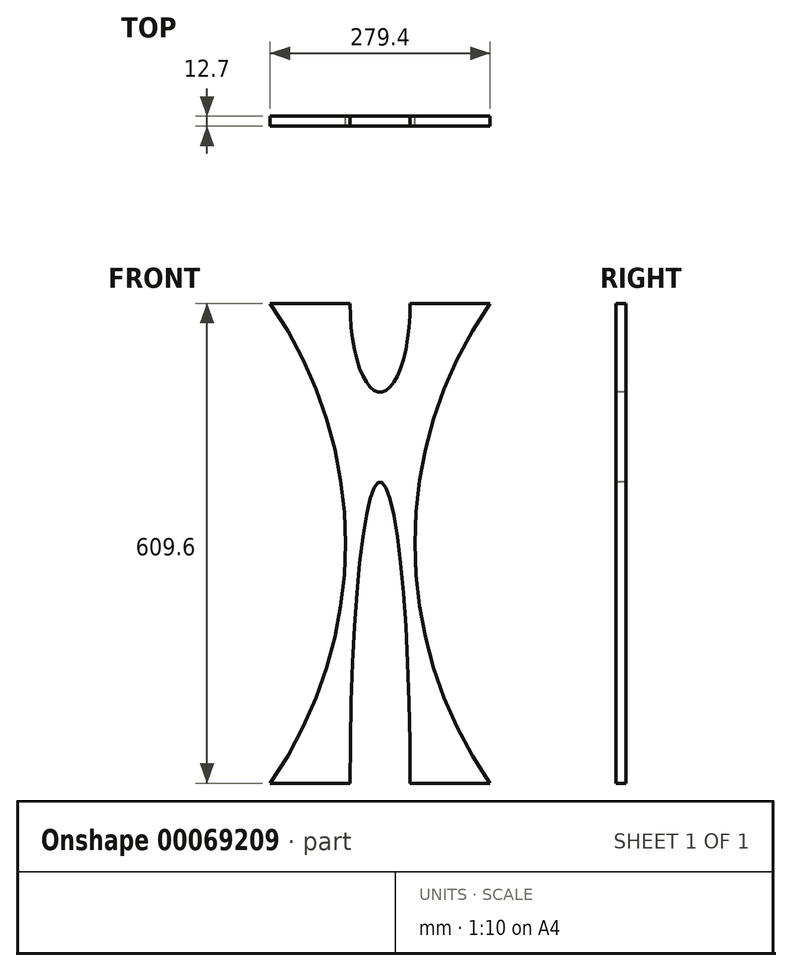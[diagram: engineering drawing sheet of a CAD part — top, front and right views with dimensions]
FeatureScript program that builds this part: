
annotation { "Feature Type Name" : "Feature", "Feature Type Description" : "" }
export const myFeature = defineFeature(function(context is Context, id is Id, definition is map)
    precondition{}
    {
        {
            var Q0;
            Q0=qCreatedBy(makeId("Front.planeOp"),FACE);
            var sketch = newSketch(context, id + "F0", { "sketchPlane" : qUnion([Q0])});
            skLineSegment(sketch, "E0", {"start": v(0, 0) * mm, "end": v(101.6, 0) * mm});
            skLineSegment(sketch, "E1", {"start": v(101.6, 609.6) * mm, "end": v(0, 609.6) * mm});
            skLineSegment(sketch, "E2", {"start": v(0, 0) * mm, "end": v(0, 704.65) * mm, "construction": true});
            skLineSegment(sketch, "E3", {"start": v(-38.1, 0) * mm, "end": v(-38.1, 704.65) * mm, "construction": true});
            skLineSegment(sketch, "E4", {"start": v(-135.6, 355.6) * mm, "end": v(135.5, 355.6) * mm, "construction": true});
            skArc(sketch, "E5", {"start": v(101.6, 609.6) * mm, "mid": v(5.94, 304.8) * mm, "end": v(101.6, 0) * mm});
            skEllipticalArc(sketch, "E6", {});
            skEllipticalArc(sketch, "E7", {});
            skLineSegment(sketch, "E8.MirrorCS", {"start": v(-177.8, 609.6) * mm, "end": v(-76.2, 609.6) * mm});
            skLineSegment(sketch, "E9.MirrorCS", {"start": v(-76.2, 0) * mm, "end": v(-177.8, 0) * mm});
            skArc(sketch, "E10.MirrorCS", {"start": v(-177.8, 609.6) * mm, "mid": v(-82.14, 304.8) * mm, "end": v(-177.8, 0) * mm});
            skEllipticalArc(sketch, "E11.MirrorCS", {});
            skEllipticalArc(sketch, "E12.MirrorCS", {});
            const initialGuessF0  = {"E6": [-0.0381, 0, 1, 0, 0.0381, 0.3830003180913211, 6.283185307179586, 1.5707963267948966], "E7": [-0.0381, 0.6096, 1, 0, 0.0381, 0.1128433488107344, 4.71238898038469, 6.283185307179586], "E11.MirrorCS": [-0.0381, 0.6096, -1, 0, 0.0381, 0.1128433488107344, 6.283185307179586, 1.5707963267948966], "E12.MirrorCS": [-0.0381, 0, -1, 0, 0.0381, 0.3830003180913211, 4.71238898038469, 6.283185307179586]};
            skSetInitialGuess(sketch, initialGuessF0);
            skSolve(sketch);
        }
        {
            var Q0;
            Q0=qSketchRegion(id+"F0",true);
            extrude(context, id + "F1", {"entities" : qUnion([Q0]), "depth" : 12.7 * mm});
        }
    });
